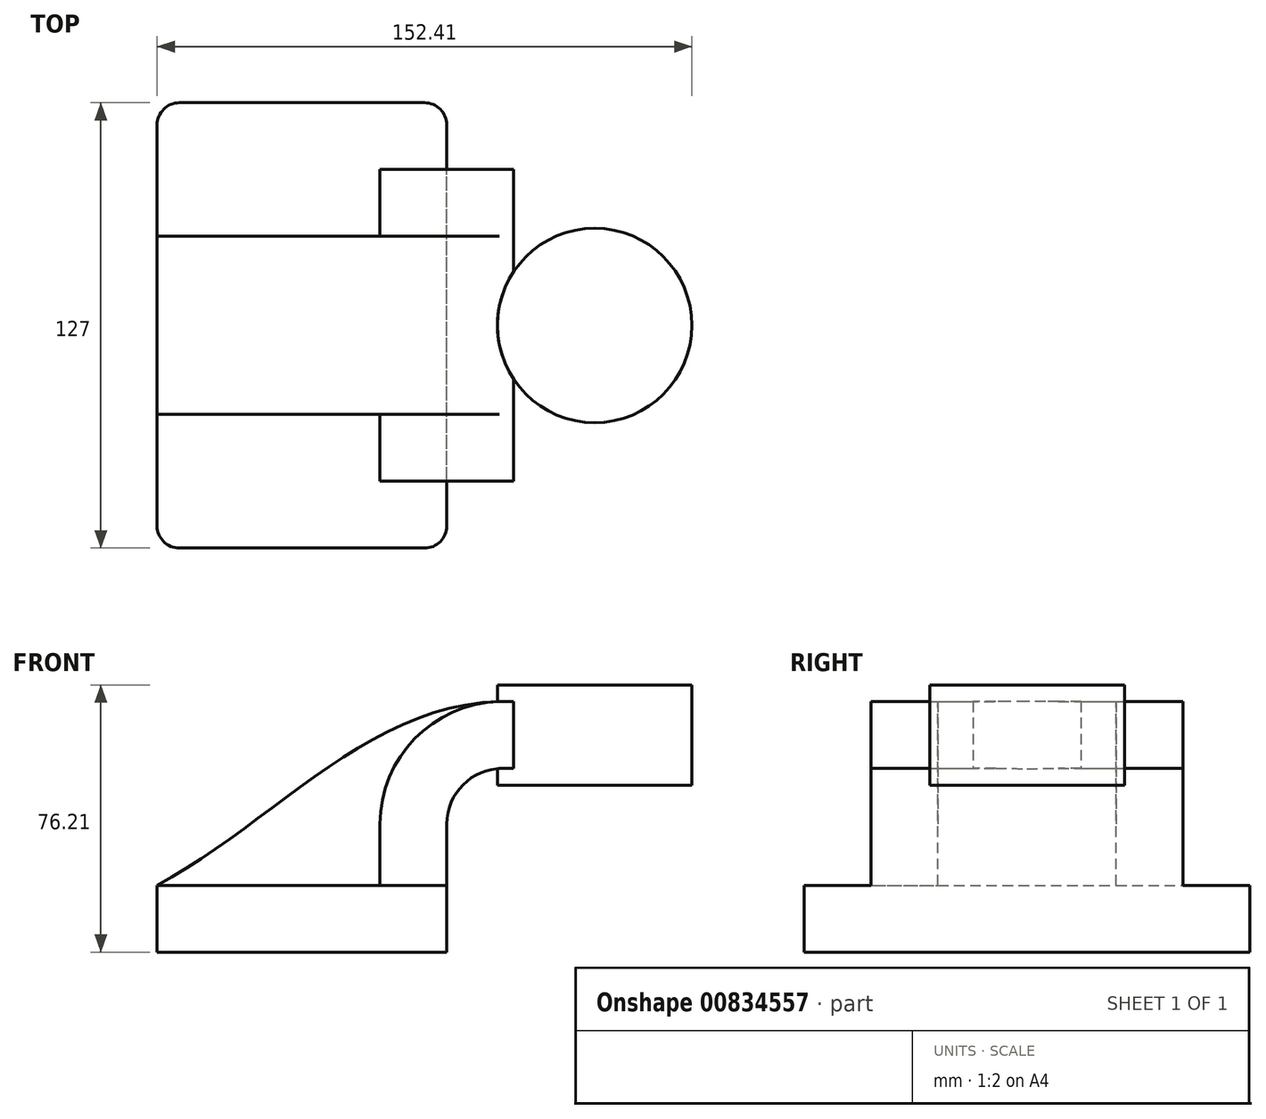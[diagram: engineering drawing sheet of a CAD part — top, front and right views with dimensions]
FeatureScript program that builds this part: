
annotation { "Feature Type Name" : "Feature", "Feature Type Description" : "" }
export const myFeature = defineFeature(function(context is Context, id is Id, definition is map)
    precondition{}
    {
        {
            var Q0;
            Q0=qCreatedBy(makeId("Front.planeOp"),FACE);
            var sketch = newSketch(context, id + "F0", { "sketchPlane" : qUnion([Q0])});
            skLineSegment(sketch, "E0.bottom", {"start": v(41.28, -9.52) * mm, "end": v(-41.28, -9.53) * mm});
            skLineSegment(sketch, "E0.top", {"start": v(41.28, 9.53) * mm, "end": v(-41.28, 9.53) * mm});
            skLineSegment(sketch, "E0.left", {"start": v(41.28, -9.52) * mm, "end": v(41.28, 9.53) * mm});
            skLineSegment(sketch, "E0.right", {"start": v(-41.28, -9.53) * mm, "end": v(-41.28, 9.53) * mm});
            skPoint(sketch, "E0.middle", {"position": v(0, 0) * mm});
            skLineSegment(sketch, "E1.bottom", {"start": v(60.32, 38.1) * mm, "end": v(111.12, 38.1) * mm});
            skLineSegment(sketch, "E1.top", {"start": v(60.32, 66.68) * mm, "end": v(111.12, 66.68) * mm});
            skLineSegment(sketch, "E1.left", {"start": v(60.32, 38.1) * mm, "end": v(60.32, 66.68) * mm});
            skLineSegment(sketch, "E1.right", {"start": v(111.12, 38.1) * mm, "end": v(111.12, 66.68) * mm});
            skPoint(sketch, "E1.middle", {"position": v(85.72, 52.39) * mm});
            skLineSegment(sketch, "E2", {"start": v(41.28, 9.53) * mm, "end": v(41.28, 26.99) * mm});
            skArc(sketch, "E3", {"start": v(41.27, 26.99) * mm, "mid": v(45.92, 38.21) * mm, "end": v(57.15, 42.86) * mm});
            skLineSegment(sketch, "E4", {"start": v(57.15, 42.86) * mm, "end": v(83.28, 42.86) * mm});
            skLineSegment(sketch, "E5.0", {"start": v(57.15, 61.91) * mm, "end": v(83.28, 61.91) * mm});
            skArc(sketch, "E5.1", {"start": v(22.23, 26.99) * mm, "mid": v(32.45, 51.68) * mm, "end": v(57.15, 61.91) * mm});
            skLineSegment(sketch, "E5.2", {"start": v(22.22, 9.53) * mm, "end": v(22.22, 26.99) * mm});
            skLineSegment(sketch, "E6", {"start": v(83.4, 38.1) * mm, "end": v(83.4, 66.68) * mm});
            skFitSpline(sketch, "E7", {"points": [v(-41.28, 9.52) * mm, v(57.15, 61.91) * mm], "startDerivative": vector(98.42, 52.39) * mm, "endDerivative": vector(114.08, 0.7) * mm});
            skSolve(sketch);
        }
        {
            var Q0;
            Q0=makeQuery(id+"F0.imprint","IMPRINT",FACE,{"disambiguationData":[TD([[makeQuery(id+"F0.imprint","IMPRINT",EDGE,{"derivedFrom":sQuery(id+"F0.wireOp",EDGE,"E0.bottom")}),-1.0]])]});
            extrude(context, id + "F1", {"entities" : qUnion([Q0]), "endBound" : BoundingType.SYMMETRIC, "depth" : 127 * mm, "offsetDistance" : 25.4 * mm});
        }
        {
            var Q0;
            {var subQ3=sQuery(id+"F0.wireOp",EDGE,"E5.2");Q0=makeQuery(id+"F0.imprint","IMPRINT",FACE,{"disambiguationData":[TD([[makeQuery(id+"F0.imprint","IMPRINT",EDGE,{"derivedFrom":subQ3}),1.0]])]});}
            extrude(context, id + "F2", {"entities" : qUnion([Q0]), "operationType" : NewBodyOperationType.ADD, "endBound" : BoundingType.SYMMETRIC, "depth" : 50.8 * mm, "offsetDistance" : 25.4 * mm});
        }
        {
            var Q0;
            {var subQ1=sQuery(id+"F0.wireOp",EDGE,"E2");Q0=makeQuery(id+"F0.imprint","IMPRINT",FACE,{"disambiguationData":[TD([[makeQuery(id+"F0.imprint","IMPRINT",EDGE,{"derivedFrom":subQ1}),1.0]])]});}
            extrude(context, id + "F3", {"entities" : qUnion([Q0]), "operationType" : NewBodyOperationType.ADD, "endBound" : BoundingType.SYMMETRIC, "depth" : 88.9 * mm, "offsetDistance" : 25.4 * mm});
        }
        {
            var Q0;
            {var subQ0=sQuery(id+"F0.wireOp",EDGE,"E1.right");Q0=makeQuery(id+"F0.imprint","IMPRINT",FACE,{"disambiguationData":[TD([[makeQuery(id+"F0.imprint","IMPRINT",EDGE,{"derivedFrom":subQ0}),1.0]])]});}
            var Q1;
            Q1=sQuery(id+"F0.wireOp",EDGE,"E6");
            revolve(context, id + "F4", {"operationType" : NewBodyOperationType.ADD, "surfaceOperationType" : NewSurfaceOperationType.NEW, "entities" : qUnion([Q0]), "axis" : qUnion([Q1]), "revolveType" : RevolveType.FULL});
        }
        {
            var Q0;
            Q0=makeQuery(id+"F1.opExtrude","CAP_EDGE",EDGE,{"disambiguationData":[OSD([sQuery(id+"F0.wireOp",EDGE,"E0.left")])],"isStart":false});
            var Q1;
            Q1=makeQuery(id+"F1.opExtrude","CAP_EDGE",EDGE,{"disambiguationData":[OSD([sQuery(id+"F0.wireOp",EDGE,"E0.right")])],"isStart":false});
            var Q2;
            Q2=makeQuery(id+"F1.opExtrude","CAP_EDGE",EDGE,{"disambiguationData":[OSD([sQuery(id+"F0.wireOp",EDGE,"E0.right")])],"isStart":true});
            var Q3;
            Q3=makeQuery(id+"F1.opExtrude","CAP_EDGE",EDGE,{"disambiguationData":[OSD([sQuery(id+"F0.wireOp",EDGE,"E0.left")])],"isStart":true});
            fillet(context, id + "F5", {"entities" : qUnion([Q0, Q1, Q2, Q3]), "radius" : 6.35 * mm, "tangentPropagation" : true, "allowEdgeOverflow" : false});
        }
    });
